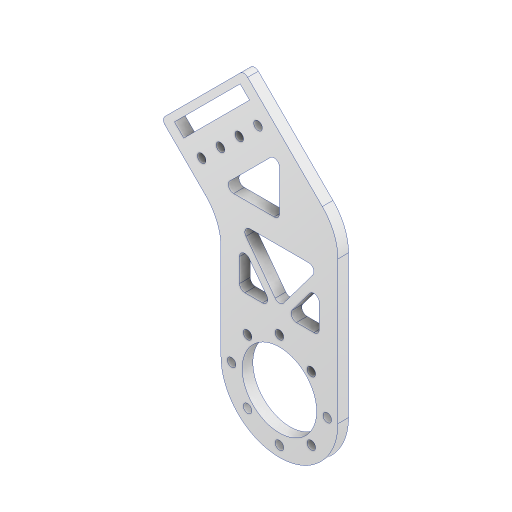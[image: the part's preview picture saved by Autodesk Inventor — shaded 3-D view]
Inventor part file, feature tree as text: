
AUTODESK INVENTOR PART (.ipt)
format: ipt  version: 2023.2 (Build 272271000, 271)  size: 380,928 bytes
history: native  units: mm
features: extrude x8, sketch x6, projected_geometry x3, fillet x2, other x1
ambient origin geometry x8: Origin, YZ Plane, XZ Plane, XY Plane, X Axis, Y Axis, Z Axis, Center Point
bodies: Body1 (feature_tree)
feature tree (20):
  other  "솔리드1"
  extrude  "돌출1"  Depth=44.0mm
  sketch  "스케치2"
  extrude  "돌출4"  Depth=18.0mm
  sketch  "스케치5"
  extrude  "돌출7"  Depth=4.0mm TaperAngle=0.0deg
  extrude  "돌출8"  Depth=80.0mm
  extrude  "돌출9"  Depth=28.0mm
  extrude  "돌출10"  Depth=4.0mm TaperAngle=0.0deg
  extrude  "돌출11"  Depth=8.0mm
  fillet  "모깎기1"  Radius=15.0mm
  extrude  "돌출12"  Depth=15.0mm
  fillet  "모깎기2"  Radius=20.0mm
  sketch  "스케치4"
  sketch  "스케치9"
  projected_geometry  "투영된 루프1"
  sketch  "스케치10"
  projected_geometry  "투영된 루프2"
  sketch  "스케치11"
  projected_geometry  "투영된 루프3"
